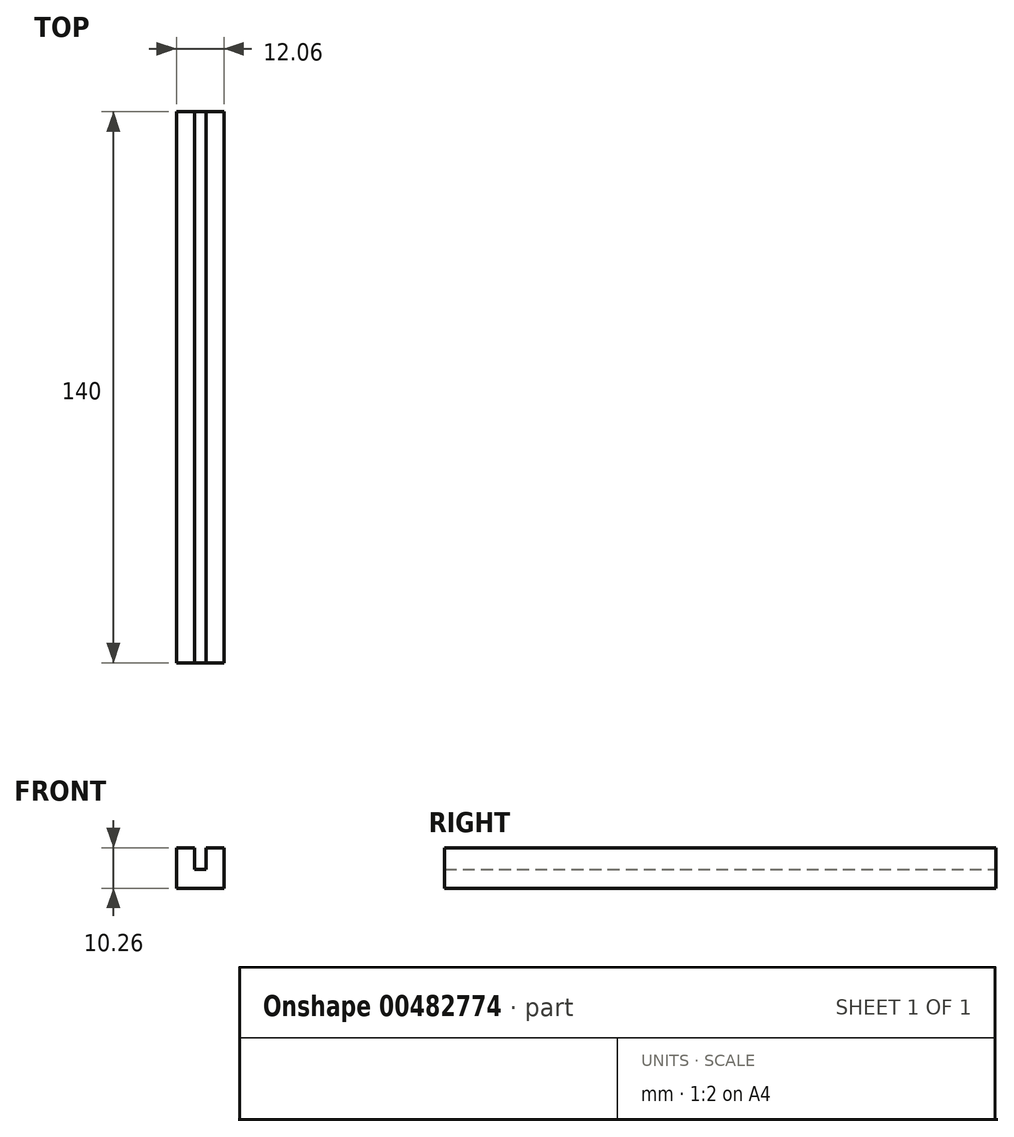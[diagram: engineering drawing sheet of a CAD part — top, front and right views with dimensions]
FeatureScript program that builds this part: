
annotation { "Feature Type Name" : "Feature", "Feature Type Description" : "" }
export const myFeature = defineFeature(function(context is Context, id is Id, definition is map)
    precondition{}
    {
        {
            var Q0;
            Q0=qCreatedBy(makeId("Front.planeOp"),FACE);
            var sketch = newSketch(context, id + "F0", { "sketchPlane" : qUnion([Q0])});
            skLineSegment(sketch, "E0", {"start": v(-1.48, 10.26) * mm, "end": v(-6.03, 10.26) * mm});
            skLineSegment(sketch, "E1", {"start": v(-6.03, 10.26) * mm, "end": v(-6.03, 0) * mm});
            skLineSegment(sketch, "E2", {"start": v(-1.48, 10.26) * mm, "end": v(-1.48, 4.76) * mm});
            skLineSegment(sketch, "E3", {"start": v(-1.48, 4.76) * mm, "end": v(0, 4.76) * mm});
            skLineSegment(sketch, "E4", {"start": v(0, 0) * mm, "end": v(-6.03, 0) * mm});
            skLineSegment(sketch, "E5.MirrorCS", {"start": v(1.48, 4.76) * mm, "end": v(0, 4.76) * mm});
            skLineSegment(sketch, "E6.MirrorCS", {"start": v(1.48, 10.26) * mm, "end": v(1.48, 4.76) * mm});
            skLineSegment(sketch, "E7.MirrorCS", {"start": v(1.48, 10.26) * mm, "end": v(6.03, 10.26) * mm});
            skLineSegment(sketch, "E8.MirrorCS", {"start": v(6.03, 10.26) * mm, "end": v(6.03, 0) * mm});
            skLineSegment(sketch, "E9.MirrorCS", {"start": v(0, 0) * mm, "end": v(6.03, 0) * mm});
            skSolve(sketch);
        }
        {
            var Q0;
            Q0=makeQuery(id+"F0.imprint","IMPRINT",FACE,{"disambiguationData":[TD([[makeQuery(id+"F0.imprint","IMPRINT",EDGE,{"derivedFrom":sQuery(id+"F0.wireOp",EDGE,"E0")}),1.0]])]});
            extrude(context, id + "F1", {"entities" : qUnion([Q0]), "depth" : 140 * mm});
        }
    });
